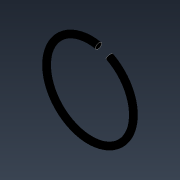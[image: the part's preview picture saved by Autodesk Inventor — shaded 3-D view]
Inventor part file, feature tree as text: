
AUTODESK INVENTOR PART (.ipt)
format: ipt  version: 2022 (Build 260153000, 153)  size: 117,248 bytes
history: native  units: mm
features: sketch x2, plane x1, sweep x1
ambient origin geometry x8: Origin, YZ Plane, XZ Plane, XY Plane, X Axis, Y Axis, Z Axis, Center Point
bodies: Solid1 (feature_tree)
feature tree (4):
  sketch  "Sketch1"  dims[d0=15.0deg d1=42.0mm]
  plane  "Work Plane1"
  sweep  "Sweep1"
  sketch  "Sketch2"  dims[d2=3.0mm d3=0.0mm d4=0.0mm]
